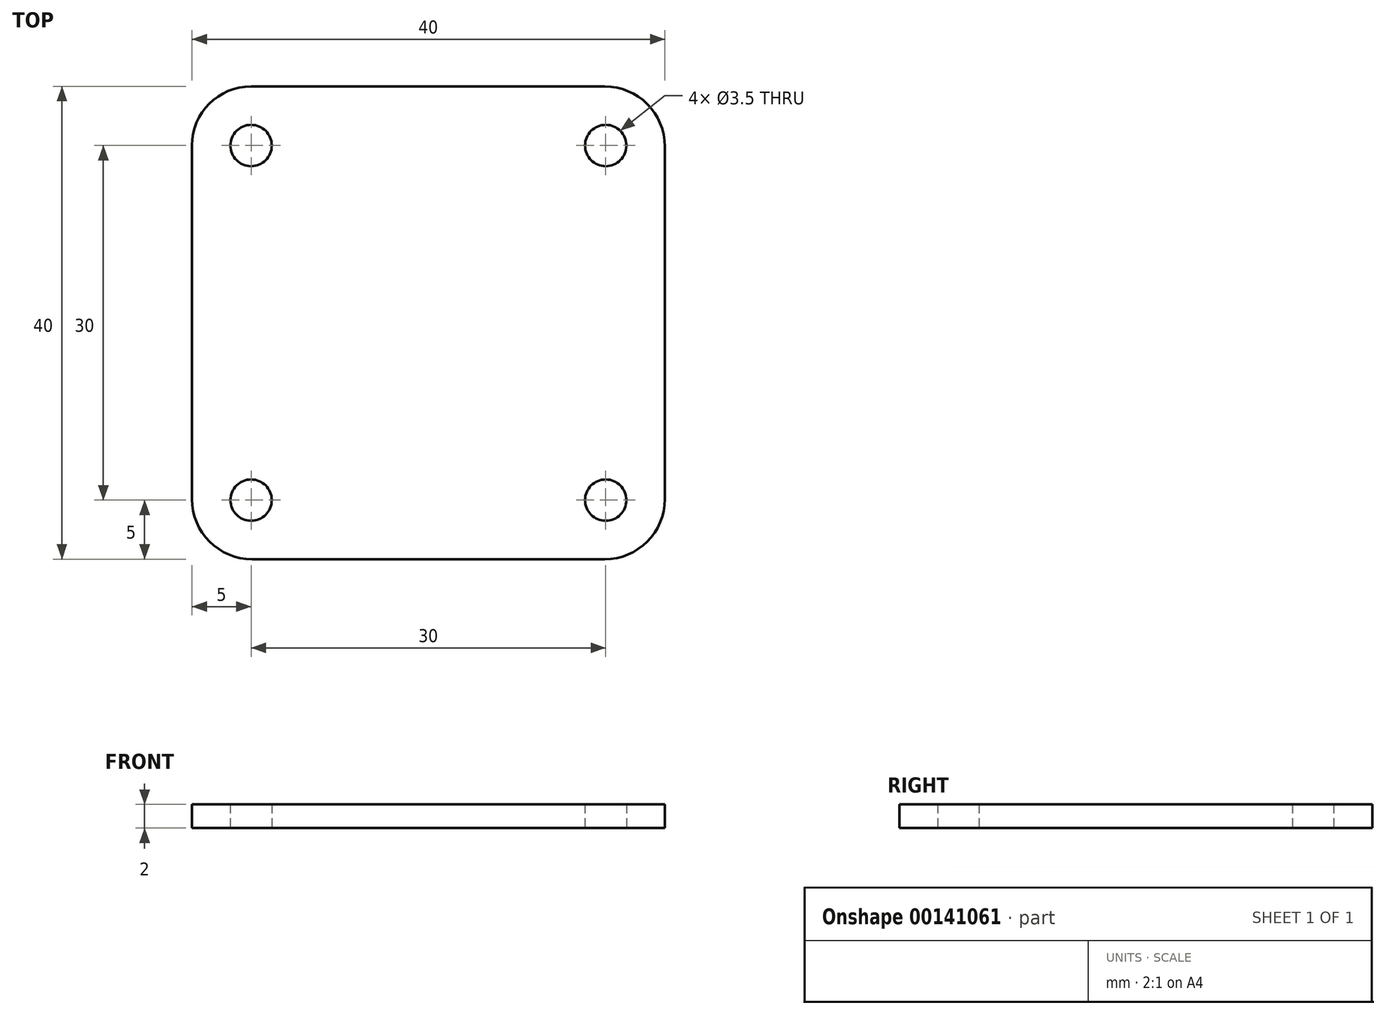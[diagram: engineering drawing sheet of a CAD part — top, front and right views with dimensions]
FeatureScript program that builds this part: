
annotation { "Feature Type Name" : "Feature", "Feature Type Description" : "" }
export const myFeature = defineFeature(function(context is Context, id is Id, definition is map)
    precondition{}
    {
        {
            var Q0;
            Q0=qCreatedBy(makeId("Top.planeOp"),FACE);
            var sketch = newSketch(context, id + "F0", { "sketchPlane" : qUnion([Q0])});
            skLineSegment(sketch, "E0.bottom", {"start": v(14.92, 20) * mm, "end": v(-15, 20) * mm});
            skLineSegment(sketch, "E0.top", {"start": v(14.92, -20) * mm, "end": v(-14.92, -20) * mm});
            skLineSegment(sketch, "E0.left", {"start": v(20, 14.92) * mm, "end": v(20, -14.92) * mm});
            skLineSegment(sketch, "E0.right", {"start": v(-20, 15) * mm, "end": v(-20, -14.92) * mm});
            skPoint(sketch, "E0.middle", {"position": v(0, 0) * mm});
            skCircle(sketch, "E1", {"center": v(-15, 15) * mm, "radius": 1.75 * mm});
            skCircle(sketch, "E2", {"center": v(15, 15) * mm, "radius": 1.75 * mm});
            skCircle(sketch, "E3", {"center": v(15, -15) * mm, "radius": 1.75 * mm});
            skCircle(sketch, "E4", {"center": v(-15, -15) * mm, "radius": 1.75 * mm});
            skLineSegment(sketch, "E5.bottom", {"start": v(15, 15) * mm, "end": v(-15, 15) * mm, "construction": true});
            skLineSegment(sketch, "E5.top", {"start": v(15, -15) * mm, "end": v(-15, -15) * mm, "construction": true});
            skLineSegment(sketch, "E5.left", {"start": v(15, 15) * mm, "end": v(15, -15) * mm, "construction": true});
            skLineSegment(sketch, "E5.right", {"start": v(-15, 15) * mm, "end": v(-15, -15) * mm, "construction": true});
            skPoint(sketch, "E6.visualSharp", {"position": v(-20, 20) * mm});
            skArc(sketch, "E6.filletArc", {"start": v(-15, 20) * mm, "mid": v(-18.54, 18.54) * mm, "end": v(-20, 15) * mm});
            skPoint(sketch, "E7.visualSharp", {"position": v(20, 20) * mm});
            skArc(sketch, "E7.filletArc", {"start": v(20, 14.92) * mm, "mid": v(18.51, 18.51) * mm, "end": v(14.92, 20) * mm});
            skPoint(sketch, "E8.visualSharp", {"position": v(20, -20) * mm});
            skArc(sketch, "E8.filletArc", {"start": v(14.92, -20) * mm, "mid": v(18.51, -18.51) * mm, "end": v(20, -14.92) * mm});
            skPoint(sketch, "E9.visualSharp", {"position": v(-20, -20) * mm});
            skArc(sketch, "E9.filletArc", {"start": v(-20, -14.92) * mm, "mid": v(-18.51, -18.51) * mm, "end": v(-14.92, -20) * mm});
            skSolve(sketch);
        }
        {
            var Q0;
            Q0 = qSketchRegion(id + "F0", true);
            extrude(context, id + "F1", {"entities" : qUnion([Q0]), "depth" : 2 * mm});
        }
    });
